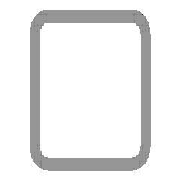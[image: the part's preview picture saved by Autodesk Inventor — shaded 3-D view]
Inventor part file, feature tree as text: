
AUTODESK INVENTOR PART (.ipt)
format: ipt  version: 2017 (Build 210142000, 142)  size: 133,632 bytes
history: native  units: mm (DEFAULTED — no unit token found)
features: other x4, plane x3, sketch x3, split x2
ambient origin geometry x8: Origin, YZ Plane, XZ Plane, XY Plane, X Axis, Y Axis, Z Axis, Center Point
bodies: Solid1 (feature_tree), Body (feature_tree)
feature tree (12):
  parser-record x1  (decoder bookkeeping rows leaked as tree rows — omitted from the tree; the rows remain in map.json)
  other  "Driven Length"
  other  "Start plane"
  other  "End plane"
  plane  "Work Plane4"
  split  "Split1"
  plane  "Work Plane5"
  split  "Split2"
  sketch  "Sketch"  dims[d10=76.2mm d11=76.2mm d12=6.35mm d13=266.7mm d14=952.5mm d15=38.1mm d16=38.1mm d17=12.7mm d18=90.0deg d19=685.8mm]
  sketch  "Sketch3"  dims[d3=685.8mm]
  plane  "Work Plane3"
  sketch  "Sketch4"  dims[d4=0.0mm]
